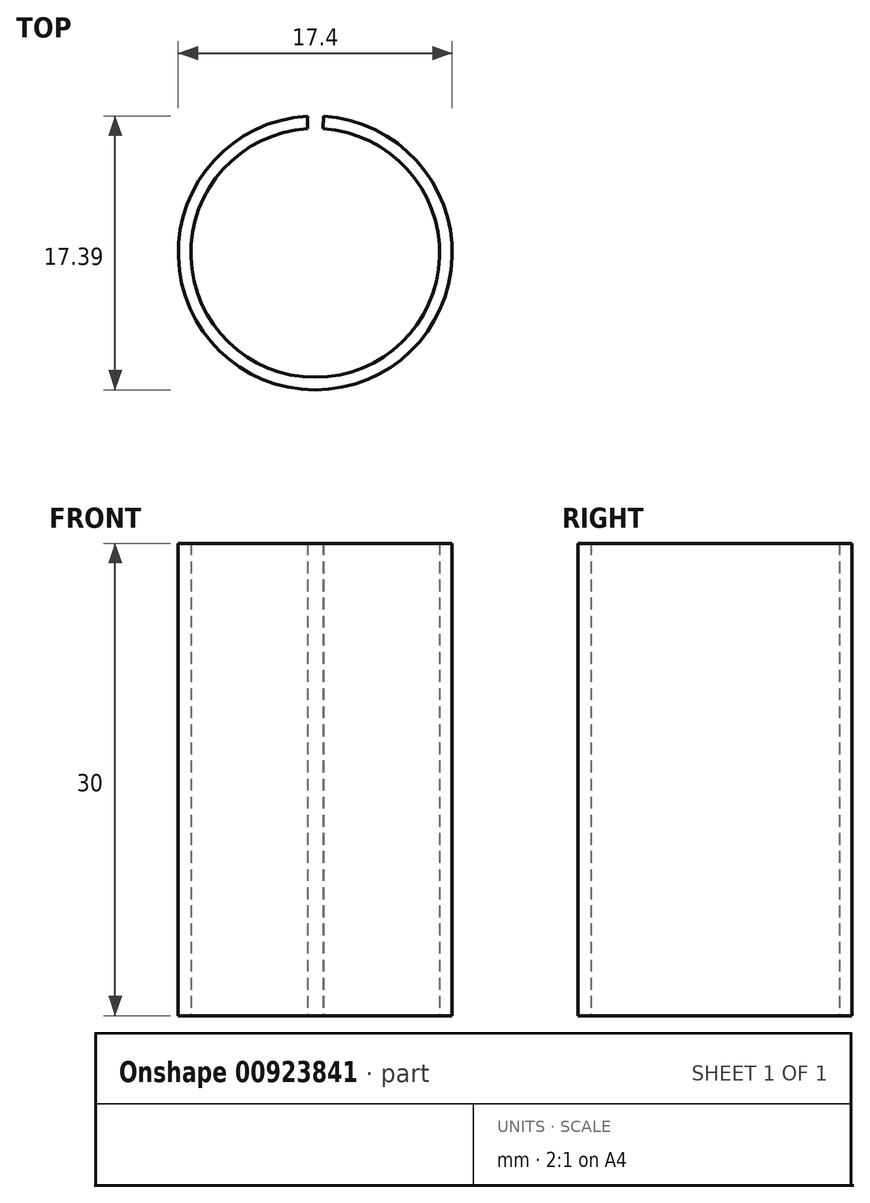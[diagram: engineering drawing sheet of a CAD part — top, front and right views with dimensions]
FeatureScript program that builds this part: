
annotation { "Feature Type Name" : "Feature", "Feature Type Description" : "" }
export const myFeature = defineFeature(function(context is Context, id is Id, definition is map)
    precondition{}
    {
        {
            var Q0;
            Q0=qCreatedBy(makeId("Top.planeOp"),FACE);
            var sketch = newSketch(context, id + "F0", { "sketchPlane" : qUnion([Q0])});
            skArc(sketch, "E0", {"start": v(-0.5, 7.88) * mm, "mid": v(0, -7.9) * mm, "end": v(0.5, 7.88) * mm});
            skArc(sketch, "E1.0", {"start": v(-0.5, 8.69) * mm, "mid": v(-0.01, -8.7) * mm, "end": v(0.52, 8.68) * mm});
            skLineSegment(sketch, "E2", {"start": v(-0.5, 8.69) * mm, "end": v(-0.5, 7.88) * mm});
            skLineSegment(sketch, "E3", {"start": v(0.5, 7.88) * mm, "end": v(0.52, 8.68) * mm});
            skSolve(sketch);
        }
        {
            var Q0;
            Q0=makeQuery(id+"F0.imprint","IMPRINT",FACE,{"disambiguationData":[TD([[makeQuery(id+"F0.imprint","IMPRINT",EDGE,{"derivedFrom":sQuery(id+"F0.wireOp",EDGE,"E0")}),-1.0]])]});
            extrude(context, id + "F1", {"entities" : qUnion([Q0]), "depth" : 30 * mm, "offsetDistance" : 25 * mm});
        }
    });
